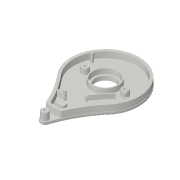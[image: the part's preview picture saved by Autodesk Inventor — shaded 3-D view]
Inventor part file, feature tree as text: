
AUTODESK INVENTOR PART (.ipt)
format: ipt  version: 2016 SP1 (Build 200210100, 210)  size: 423,936 bytes
history: native  units: mm
features: extrude x12, sketch x12, projected_geometry x10, fillet x3
ambient origin geometry x8: Origin, YZ Plane, XZ Plane, XY Plane, X Axis, Y Axis, Z Axis, Center Point
bodies: Volumenkörper1 (feature_tree)
feature tree (37):
  extrude  "Extrusion1"  Depth=29.7mm
  extrude  "Extrusion2"  Depth=3.6mm
  extrude  "Extrusion3"  Depth=55.0mm
  extrude  "Extrusion4"  Depth=1.8mm TaperAngle=0.0deg
  extrude  "Extrusion5"  Depth=1.8mm TaperAngle=0.0deg
  extrude  "Extrusion6"  Depth=1.0mm
  fillet  "Rundung1"  Radius=3.2mm
  extrude  "Extrusion7"  Depth=10.4mm
  extrude  "Extrusion8"  Depth=3.0mm
  extrude  "Extrusion9"  Depth=1.0mm
  extrude  "Extrusion10"  Depth=1.0mm
  fillet  "Rundung3"  Radius=8.7mm
  extrude  "Extrusion11"  Depth=2.4mm
  fillet  "Rundung4"  Radius=35.4mm
  extrude  "Extrusion12"  Depth=55.0mm
  sketch  "Skizze1"  dims[d0=27.3mm d1=29.7mm]
  sketch  "Skizze2"  dims[d2=43.0mm d3=3.6mm]
  sketch  "Skizze3"  dims[d4=55.0mm d5=55.0mm]
  projected_geometry  "Projizierte Kontur1"
  sketch  "Skizze4"  dims[d6=1.039976mm d7=1.8mm d8=0.0mm]
  sketch  "Skizze5"  dims[d9=8.5mm d10=1.8mm d11=0.0mm]
  sketch  "Skizze6"  dims[d12=3.0mm d13=1.0mm d14=3.2mm d15=0.0mm]
  projected_geometry  "Projizierte Kontur2"
  sketch  "Skizze7"  dims[d16=11.4mm d17=10.4mm]
  projected_geometry  "Projizierte Kontur3"
  projected_geometry  "Projizierte Kontur4"
  sketch  "Skizze8"  dims[d18=2.2mm d19=0.0mm d20=3.0mm]
  projected_geometry  "Projizierte Kontur5"
  sketch  "Skizze9"  dims[d21=3.0mm d22=1.0mm]
  projected_geometry  "Projizierte Kontur6"
  projected_geometry  "Projizierte Kontur7"
  sketch  "Skizze10"  dims[d23=1.0mm d24=17.4mm d25=8.7mm]
  projected_geometry  "Projizierte Kontur8"
  sketch  "Skizze11"  dims[d26=2.4mm d27=0.0mm d28=27.3mm d29=35.4mm]
  projected_geometry  "Projizierte Kontur9"
  sketch  "Skizze12"  dims[d30=4.6mm d32=55.0mm d33=55.0mm d34=55.0mm d35=37.7mm d36=2.6mm d37=0.0mm d38=1.0mm d40=1.1mm d41=1.1mm d42=1.1mm d43=6.8mm d44=2.65mm d45=2.8mm d46=2.8mm d47=5.3mm d48=2.3mm d49=3.7mm d50=0.0mm d51=3.9mm d52=2.2mm d53=33.0mm d54=4.0mm d55=0.0mm d56=8.3mm d57=5.3mm d58=9.075712mm d59=3.0mm d60=0.5mm d61=0.5mm d62=0.8mm d63=3.4mm d64=4.2mm d65=0.6mm d66=0.6mm d67=0.6mm d68=2.4mm d69=2.4mm d70=1.0mm d71=2.0mm d72=0.0mm d73=30.0mm d74=3.9mm d75=1.8mm d76=55.0mm d77=55.0mm d78=55.0mm d79=2.0mm d80=0.0mm d81=1.5mm d82=3.6mm d83=2.0mm d84=0.0mm d85=0.5mm d86=0.6mm d88=0.6mm d89=2.4mm d90=0.0mm d91=0.6mm]
  projected_geometry  "Projizierte Kontur10"
